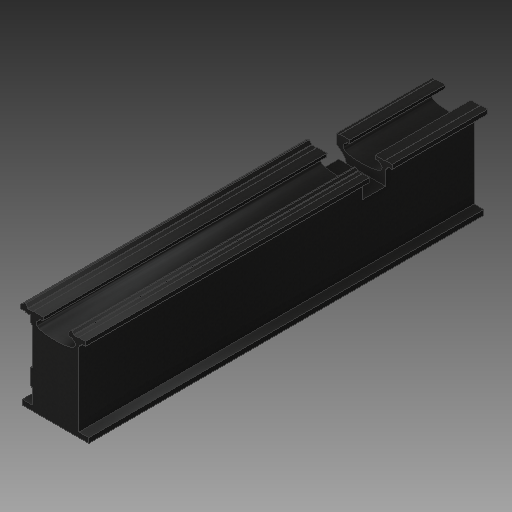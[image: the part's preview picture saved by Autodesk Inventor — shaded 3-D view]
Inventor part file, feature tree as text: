
AUTODESK INVENTOR PART (.ipt)
format: ipt  version: 2018 (Build 220112000, 112)  size: 444,416 bytes
history: native  units: in
note: dims shown in document units (in); Inventor stores cm internally (conversion verified against a paired STEP export)
features: extrude x11, sketch x11, reference x6, plane x3, chamfer x1
ambient origin geometry x8: Origin, YZ Plane, XZ Plane, XY Plane, X Axis, Y Axis, Z Axis, Center Point
bodies: Solid1 (feature_tree)
feature tree (32):
  extrude  "Extrusion1"  TaperAngle=150.0deg  [1 undecoded]
  chamfer  "Chamfer1"  Distance=0.9921in
  plane  "Work Plane3"
  extrude  "Extrusion2"  Depth=0.5118in
  extrude  "Extrusion3"  Depth=0.5118in
  extrude  "Extrusion4"  Depth=0.5118in
  extrude  "Extrusion5"  TaperAngle=120.0deg  [1 undecoded]
  extrude  "Extrusion6"  Depth=0.1575in
  extrude  "Extrusion7"  Depth=0.5118in
  extrude  "Extrusion8"  Depth=0.5118in
  plane  "Work Plane4"
  plane  "Work Plane5"
  extrude  "Extrusion9"  Depth=0.5118in
  extrude  "Extrusion10"  Depth=0.5118in
  extrude  "Extrusion11"  Depth=0.5118in
  sketch  "Sketch1"  dims[d0=0.4331in d1=150.0deg]
  sketch  "Sketch2"  dims[d2=0.3937in]
  sketch  "Sketch3"  dims[d3=0.4606in]
  sketch  "Sketch4"  dims[d4=0.4961in]
  sketch  "Sketch5"  dims[d5=0.962in]
  sketch  "Sketch6"  dims[d6=0.1496in]
  sketch  "Sketch8"  dims[d7=0.4016in]
  sketch  "Sketch9"  dims[d8=0.962in]
  sketch  "Sketch10"  dims[d9=0.126in]
  sketch  "Sketch11"  dims[d10=0.6339in]
  sketch  "Sketch12"  dims[d11=0.0787in d12=0.9921in d13=0.6181in d14=0.5787in d15=0.315in d16=120.0deg d17=0.1575in d18=2.4409in d19=8.0315in d22=3.6299in d24=0.5in d25=1.4252in d26=180.0deg d27=0.0787in d28=0.748in d29=0.0787in d30=0.5197in d31=0.962in d32=0.1811in d33=0.6299in d34=0.962in d35=0.5512in d36=0.5512in d37=90.0deg d38=0.1181in d39=60.0deg d40=0.685in d41=0.8858in d43=5.2953in d44=90.0deg d46=2.185in d47=90.0deg d50=90.0deg d51=1.378in d52=180.0deg d53=0.7087in d54=90.0deg d55=1.378in d57=0.7087in d59=180.0deg d60=0.315in d61=120.0deg d62=2.4409in d63=55.9055in d64=0.0in d65=0.1575in d66=0.0787in d67=45.0deg d68=40.1575in d69=3.2283in d70=3.4528in d71=55.9055in d72=0.0in d73=55.9055in d74=0.0in d75=55.9055in d76=0.0in d77=3.3465in d78=1.2205in d79=1.7323in d80=55.9055in d81=0.0in d82=1.0236in d83=0.0in d84=0.315in d85=0.315in d86=0.7283in d87=0.5512in d88=0.5118in d89=0.3937in d90=0.0in d91=0.315in d92=0.315in d93=6.7717in d94=0.9449in d95=0.5512in d96=0.7874in d97=0.0in d98=0.2756in d99=0.3937in d100=0.0in d101=5.5118in d102=1.9685in d103=0.2756in d104=1.5748in d105=0.0787in d106=0.0in d107=0.7874in d108=0.0in d109=0.0787in d110=0.3937in d111=1.2205in d112=0.2362in d113=0.2362in d114=1.0236in d116=0.5118in d117=3.189in]
  reference  "Reference1"
  reference  "Reference2"
  reference  "Reference3"
  reference  "Reference4"
  reference  "Reference5"
  reference  "Reference6"
note: 2 required parameter values undecoded (feature->parameter linkage not recoverable at this tier; creation-order binding heuristic only, values carry confidence <= 0.55)
